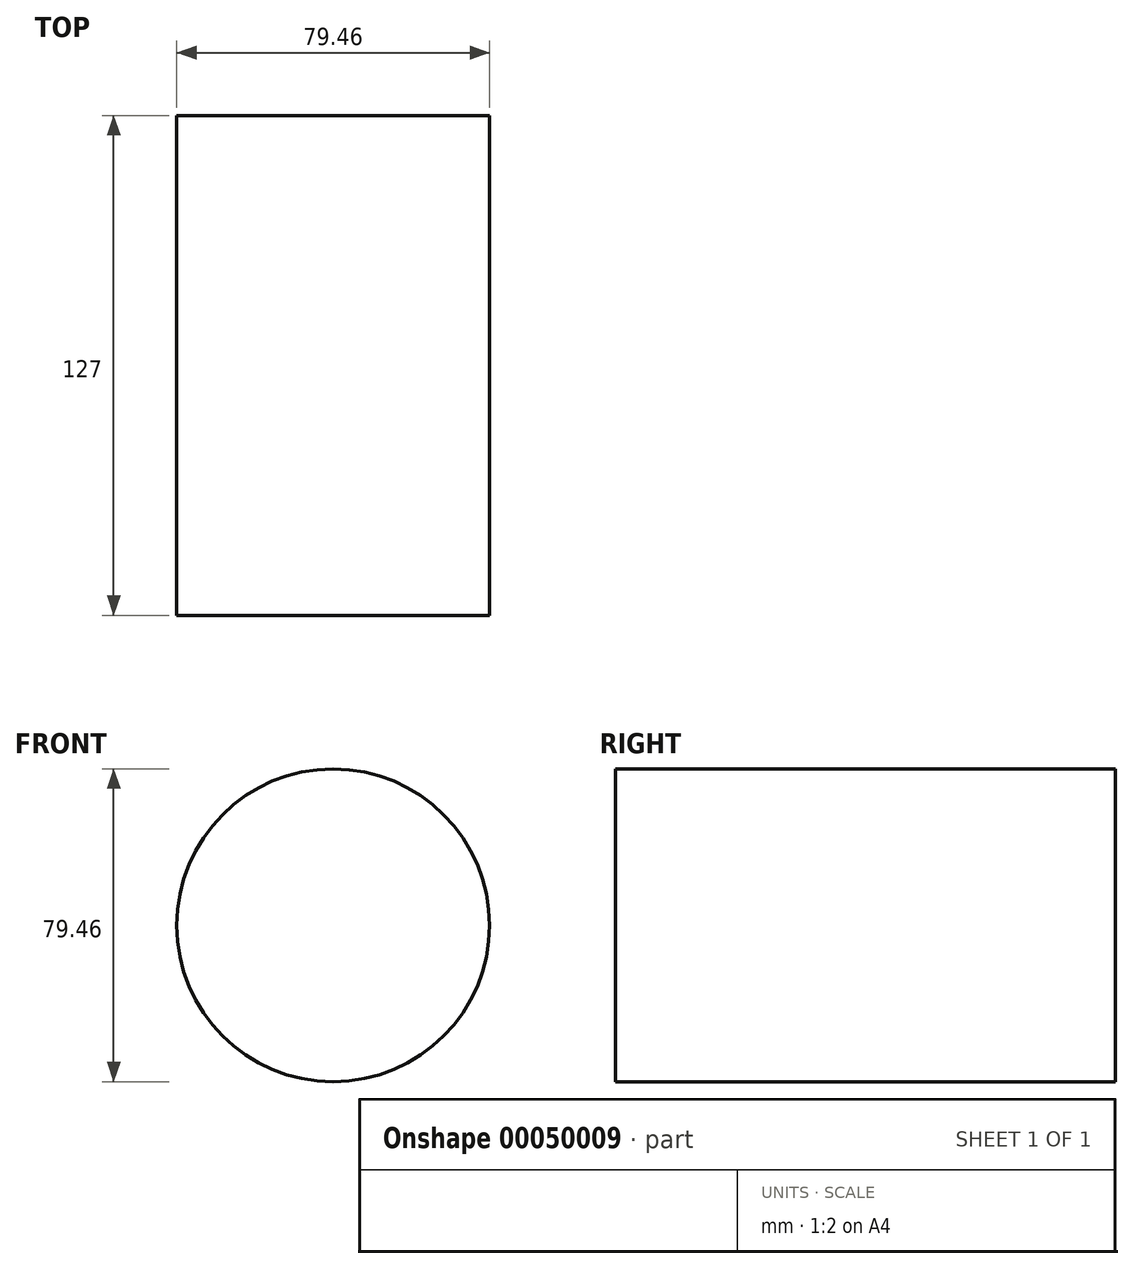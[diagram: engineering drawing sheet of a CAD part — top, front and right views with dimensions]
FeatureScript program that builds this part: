
annotation { "Feature Type Name" : "Feature", "Feature Type Description" : "" }
export const myFeature = defineFeature(function(context is Context, id is Id, definition is map)
    precondition{}
    {
        {
            var Q0;
            Q0=qCreatedBy(makeId("Front.planeOp"),FACE);
            var sketch = newSketch(context, id + "F0", { "sketchPlane" : qUnion([Q0])});
            skCircle(sketch, "E0", {"center": v(0, 0) * mm, "radius": 39.73 * mm});
            skSolve(sketch);
        }
        {
            var Q0;
            Q0=makeQuery(id+"F0.imprint","IMPRINT",FACE,{"disambiguationData":[TD([[makeQuery(id+"F0.imprint","IMPRINT",EDGE,{"derivedFrom":sQuery(id+"F0.wireOp",EDGE,"E0")}),1.0]])]});
            extrude(context, id + "F1", {"entities" : qUnion([Q0]), "depth" : 127 * mm});
        }
    });
